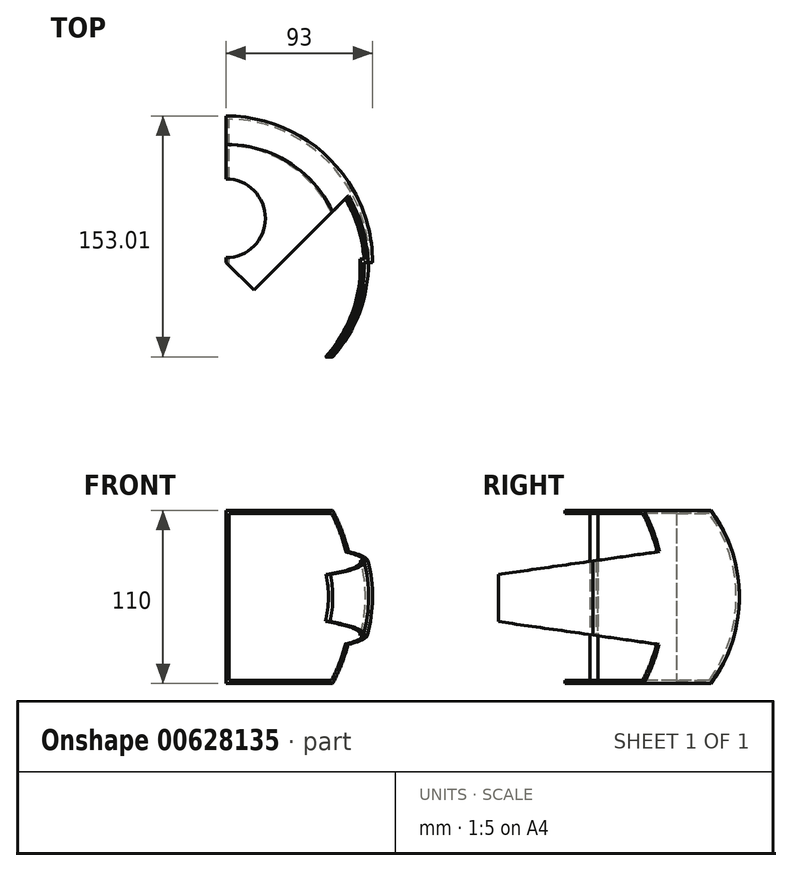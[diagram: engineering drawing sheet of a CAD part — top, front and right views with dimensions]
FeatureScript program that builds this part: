
annotation { "Feature Type Name" : "Feature", "Feature Type Description" : "" }
export const myFeature = defineFeature(function(context is Context, id is Id, definition is map)
    precondition{}
    {
        {
            var Q0;
            Q0=qCreatedBy(makeId("Right.planeOp"),FACE);
            var sketch = newSketch(context, id + "F0", { "sketchPlane" : qUnion([Q0])});
            skLineSegment(sketch, "E0", {"start": v(0, 0) * mm, "end": v(0, 55) * mm});
            skLineSegment(sketch, "E1", {"start": v(0, 55) * mm, "end": v(-75, 55) * mm});
            skArc(sketch, "E2", {"start": v(-75, 55) * mm, "mid": v(-93, 0) * mm, "end": v(-75, -55) * mm});
            skLineSegment(sketch, "E3.MirrorCS", {"start": v(0, -55) * mm, "end": v(-75, -55) * mm});
            skLineSegment(sketch, "E4.MirrorCS", {"start": v(0, 0) * mm, "end": v(0, -55) * mm});
            skSolve(sketch);
        }
        {
            var Q0;
            Q0=makeQuery(id+"F0.imprint","IMPRINT",FACE,{"disambiguationData":[TD([[makeQuery(id+"F0.imprint","IMPRINT",EDGE,{"derivedFrom":sQuery(id+"F0.wireOp",EDGE,"E0")}),1.0]])]});
            var Q1;
            Q1=sQuery(id+"F0.wireOp",EDGE,"E0");
            revolve(context, id + "F1", {"entities" : qUnion([Q0]), "axis" : qUnion([Q1]), "revolveType" : RevolveType.ONE_DIRECTION, "angle" : 180 * degree});
        }
        {
            var Q0;
            Q0=makeQuery(id+"F1.opRevolve","SWEPT_FACE",FACE,{"disambiguationData":[OSD([sQuery(id+"F0.wireOp",EDGE,"E3.MirrorCS")])]});
            var sketch = newSketch(context, id + "F2", { "sketchPlane" : qUnion([Q0])});
            skLineSegment(sketch, "E5", {"start": v(0, 0) * mm, "end": v(17.68, 17.68) * mm});
            skLineSegment(sketch, "E6", {"start": v(17.68, 17.68) * mm, "end": v(115.73, -80.38) * mm});
            skLineSegment(sketch, "E7", {"start": v(0, 0) * mm, "end": v(-101.1, 0) * mm});
            skLineSegment(sketch, "E8", {"start": v(-101.1, 0) * mm, "end": v(-101.1, 108.21) * mm});
            skLineSegment(sketch, "E9", {"start": v(-101.1, 108.21) * mm, "end": v(115.73, 108.21) * mm});
            skLineSegment(sketch, "E10", {"start": v(115.73, 108.21) * mm, "end": v(115.73, -80.38) * mm});
            skPoint(sketch, "E11.end.orphan", {"position": v(115.73, -110.8) * mm});
            skSolve(sketch);
        }
        {
            var Q0;
            Q0 = qSketchRegion(id + "F2", true);
            extrude(context, id + "F3", {"entities" : qUnion([Q0]), "operationType" : NewBodyOperationType.REMOVE, "endBound" : BoundingType.THROUGH_ALL, "oppositeDirection" : true, "depth" : 25 * mm, "offsetDistance" : 25 * mm});
        }
        {
            var Q0;
            Q0=qCreatedBy(makeId("Right.planeOp"),FACE);
            cPlane(context, id + "F4", {"entities" : qUnion([Q0]), "cplaneType" : CPlaneType.OFFSET, "offset" : 100 * mm, "width" : 150 * mm, "height" : 150 * mm});
        }
        {
            var Q0;
            Q0=qCreatedBy(id+"F4.planeOp",FACE);
            var sketch = newSketch(context, id + "F5", { "sketchPlane" : qUnion([Q0])});
            skLineSegment(sketch, "E12", {"start": v(45.67, 29.31) * mm, "end": v(45.67, -30.69) * mm});
            skLineSegment(sketch, "E13", {"start": v(-60, -0.69) * mm, "end": v(-60, 14.31) * mm});
            skLineSegment(sketch, "E14", {"start": v(0, -0.69) * mm, "end": v(45.67, -0.69) * mm});
            skLineSegment(sketch, "E15", {"start": v(-60, 14.31) * mm, "end": v(45.67, 29.31) * mm});
            skLineSegment(sketch, "E16.MirrorCS", {"start": v(-60, -0.69) * mm, "end": v(-60, -15.69) * mm});
            skLineSegment(sketch, "E17.MirrorCS", {"start": v(-60, -15.69) * mm, "end": v(45.67, -30.69) * mm});
            skSolve(sketch);
        }
        {
            var Q0;
            Q0 = qSketchRegion(id + "F5", true);
            var Q1;
            Q1=makeQuery(id+"F1.opRevolve","CAP_FACE",FACE,{"disambiguationData":[OSD([sQuery(id+"F0.wireOp",EDGE,"E0"),sQuery(id+"F0.wireOp",EDGE,"E1"),sQuery(id+"F0.wireOp",EDGE,"E2"),sQuery(id+"F0.wireOp",EDGE,"E3.MirrorCS"),sQuery(id+"F0.wireOp",EDGE,"E4.MirrorCS")])],"isStart":false});
            extrude(context, id + "F6", {"entities" : qUnion([Q0]), "operationType" : NewBodyOperationType.ADD, "endBound" : BoundingType.UP_TO_SURFACE, "oppositeDirection" : true, "depth" : 25 * mm, "endBoundEntityFace" : qUnion([Q1]), "offsetDistance" : 25 * mm});
        }
        {
            var Q0;
            Q0=qCreatedBy(makeId("Right.planeOp"),FACE);
            var sketch = newSketch(context, id + "F7", { "sketchPlane" : qUnion([Q0])});
            skArc(sketch, "E18", {"start": v(-155.56, 55) * mm, "mid": v(-165, 0) * mm, "end": v(-155.56, -55) * mm});
            skArc(sketch, "E19", {"start": v(-75, 55) * mm, "mid": v(-93, 0) * mm, "end": v(-75, -55) * mm});
            skLineSegment(sketch, "E20", {"start": v(-75, -55) * mm, "end": v(-155.56, -55) * mm});
            skLineSegment(sketch, "E21", {"start": v(-75, 55) * mm, "end": v(-155.56, 55) * mm});
            skLineSegment(sketch, "E22", {"start": v(0, 0) * mm, "end": v(0, 118.14) * mm});
            skSolve(sketch);
        }
        {
            var Q0;
            Q0=makeQuery(id+"F7.imprint","IMPRINT",FACE,{"disambiguationData":[TD([[makeQuery(id+"F7.imprint","IMPRINT",EDGE,{"derivedFrom":sQuery(id+"F7.wireOp",EDGE,"E18")}),1.0]])]});
            var Q1;
            Q1=sQuery(id+"F7.wireOp",EDGE,"E22");
            revolve(context, id + "F8", {"operationType" : NewBodyOperationType.REMOVE, "entities" : qUnion([Q0]), "axis" : qUnion([Q1]), "revolveType" : RevolveType.FULL, "oppositeDirection" : true});
        }
        {
            var Q0;
            Q0=makeQuery(id+"F1.opRevolve","SWEPT_FACE",FACE,{"disambiguationData":[OSD([sQuery(id+"F0.wireOp",EDGE,"E3.MirrorCS")])]});
            var sketch = newSketch(context, id + "F9", { "sketchPlane" : qUnion([Q0])});
            skLineSegment(sketch, "E23", {"start": v(0, 0) * mm, "end": v(73.48, 73.48) * mm});
            skLineSegment(sketch, "E24", {"start": v(73.48, 73.48) * mm, "end": v(-33.58, 73.48) * mm});
            skLineSegment(sketch, "E25", {"start": v(-33.58, 73.48) * mm, "end": v(-33.58, 0) * mm});
            skLineSegment(sketch, "E26", {"start": v(-33.58, 0) * mm, "end": v(0, 0) * mm});
            skSolve(sketch);
        }
        {
            var Q0;
            Q0 = qSketchRegion(id + "F9", true);
            extrude(context, id + "F10", {"entities" : qUnion([Q0]), "operationType" : NewBodyOperationType.REMOVE, "endBound" : BoundingType.THROUGH_ALL, "oppositeDirection" : true, "depth" : 25 * mm, "offsetDistance" : 25 * mm});
        }
        {
            var Q0;
            Q0=qCreatedBy(makeId("Right.planeOp"),FACE);
            var sketch = newSketch(context, id + "F11", { "sketchPlane" : qUnion([Q0])});
            skArc(sketch, "E27", {"start": v(-71.87, 55) * mm, "mid": v(-90.5, 0) * mm, "end": v(-71.87, -55) * mm});
            skArc(sketch, "E28", {"start": v(-106.65, 55) * mm, "mid": v(-120, 0) * mm, "end": v(-106.65, -55) * mm});
            skLineSegment(sketch, "E29", {"start": v(-71.87, 55) * mm, "end": v(-106.65, 55) * mm});
            skLineSegment(sketch, "E30", {"start": v(-71.87, -55) * mm, "end": v(-106.65, -55) * mm});
            skLineSegment(sketch, "E31", {"start": v(0, 0) * mm, "end": v(0, 84.87) * mm});
            skSolve(sketch);
        }
        {
            var Q0;
            Q0 = qSketchRegion(id + "F11", true);
            var Q1;
            Q1=sQuery(id+"F11.wireOp",EDGE,"E31");
            revolve(context, id + "F12", {"operationType" : NewBodyOperationType.REMOVE, "entities" : qUnion([Q0]), "axis" : qUnion([Q1]), "revolveType" : RevolveType.ONE_DIRECTION, "angle" : 90 * degree});
        }
        {
            var Q0;
            Q0=makeQuery(id+"F1.opRevolve","SWEPT_FACE",FACE,{"disambiguationData":[OSD([sQuery(id+"F0.wireOp",EDGE,"E3.MirrorCS")])]});
            var sketch = newSketch(context, id + "F13", { "sketchPlane" : qUnion([Q0])});
            skCircle(sketch, "E32", {"center": v(0, -28) * mm, "radius": 25 * mm});
            skSolve(sketch);
        }
        {
            var Q0;
            Q0 = qSketchRegion(id + "F13", true);
            extrude(context, id + "F14", {"entities" : qUnion([Q0]), "operationType" : NewBodyOperationType.REMOVE, "endBound" : BoundingType.THROUGH_ALL, "oppositeDirection" : true, "depth" : 25 * mm, "offsetDistance" : 25 * mm});
        }
        {
            var Q0;
            Q0=makeQuery(id+"F6.opExtrude","SWEPT_FACE",FACE,{"disambiguationData":[OSD([sQuery(id+"F5.wireOp",EDGE,"E13"),sQuery(id+"F5.wireOp",EDGE,"E16.MirrorCS")])]});
            var Q1;
            {var subQ1=sQuery(id+"F0.wireOp",EDGE,"E3.MirrorCS");var subQ3=sQuery(id+"F0.wireOp",EDGE,"E1");var subQ8=makeQuery(id+"F3.boolean.opBoolean","COPY",FACE,{"derivedFrom":makeQuery(id+"F3.opExtrude","SWEPT_FACE",FACE,{"disambiguationData":[OSD([sQuery(id+"F2.wireOp",EDGE,"E5")])]})});Q1=makeQuery(id+"F10.boolean.opBoolean","MERGE",FACE,{"derivedFrom":[makeQuery(id+"F6.boolean.opBoolean","SPLIT",FACE,{"disambiguationData":[TD([makeQuery(id+"F1.opRevolve","SWEPT_FACE",FACE,{"disambiguationData":[OSD([subQ1])]})])],"derivedFrom":subQ8}),makeQuery(id+"F6.boolean.opBoolean","SPLIT",FACE,{"disambiguationData":[TD([makeQuery(id+"F1.opRevolve","SWEPT_FACE",FACE,{"disambiguationData":[OSD([subQ3])]})])],"derivedFrom":subQ8}),makeQuery(id+"F10.opExtrude","SWEPT_FACE",FACE,{"disambiguationData":[OSD([sQuery(id+"F9.wireOp",EDGE,"E23")])]})]});}
            var Q2;
            Q2=makeQuery(id+"F6.opExtrude","SWEPT_FACE",FACE,{"disambiguationData":[OSD([sQuery(id+"F5.wireOp",EDGE,"E17.MirrorCS")])]});
            var Q3;
            Q3=makeQuery(id+"F6.boolean.opBoolean","SPLIT",FACE,{"disambiguationData":[TD([makeQuery(id+"F1.opRevolve","SWEPT_FACE",FACE,{"disambiguationData":[OSD([sQuery(id+"F0.wireOp",EDGE,"E1")])]})])],"derivedFrom":makeQuery(id+"F3.boolean.opBoolean","COPY",FACE,{"derivedFrom":makeQuery(id+"F3.opExtrude","SWEPT_FACE",FACE,{"disambiguationData":[OSD([sQuery(id+"F2.wireOp",EDGE,"E6")])]})})});
            var Q4;
            Q4=makeQuery(id+"F6.boolean.opBoolean","SPLIT",FACE,{"disambiguationData":[TD([makeQuery(id+"F1.opRevolve","SWEPT_FACE",FACE,{"disambiguationData":[OSD([sQuery(id+"F0.wireOp",EDGE,"E3.MirrorCS")])]})])],"derivedFrom":makeQuery(id+"F3.boolean.opBoolean","COPY",FACE,{"derivedFrom":makeQuery(id+"F3.opExtrude","SWEPT_FACE",FACE,{"disambiguationData":[OSD([sQuery(id+"F2.wireOp",EDGE,"E6")])]})})});
            var Q5;
            Q5=makeQuery(id+"F6.opExtrude","SWEPT_FACE",FACE,{"disambiguationData":[OSD([sQuery(id+"F5.wireOp",EDGE,"E15")])]});
            var Q6;
            Q6=makeQuery(id+"F14.boolean.opBoolean","COPY",FACE,{"derivedFrom":makeQuery(id+"F14.opExtrude","SWEPT_FACE",FACE,{"disambiguationData":[OSD([sQuery(id+"F13.wireOp",EDGE,"E32")])]})});
            shell(context, id + "F15", {"entities" : qUnion([Q0, Q1, Q2, Q3, Q4, Q5, Q6]), "thickness" : 2 * mm});
        }
    });
